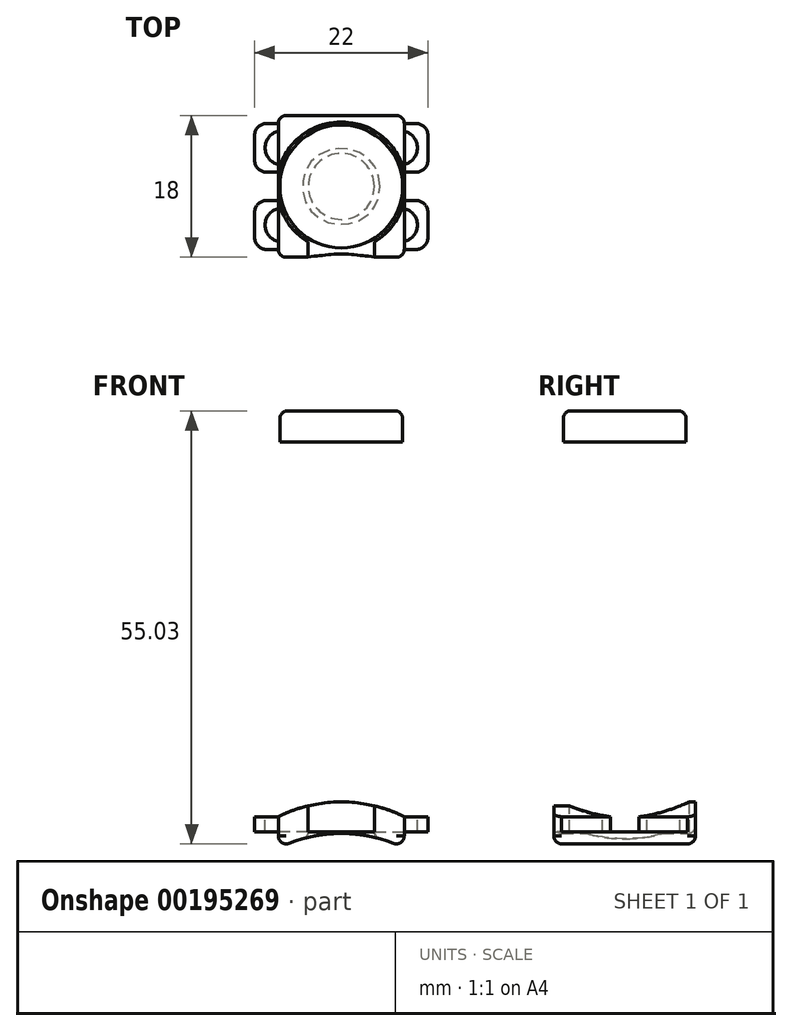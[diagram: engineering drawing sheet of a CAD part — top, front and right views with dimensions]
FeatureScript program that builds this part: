
annotation { "Feature Type Name" : "Feature", "Feature Type Description" : "" }
export const myFeature = defineFeature(function(context is Context, id is Id, definition is map)
    precondition{}
    {
        {
            var Q0;
            Q0=qCreatedBy(makeId("Front.planeOp"),FACE);
            var sketch = newSketch(context, id + "F0", { "sketchPlane" : qUnion([Q0])});
            skLineSegment(sketch, "E0.left", {"start": v(8, 1.57) * mm, "end": v(8, -1.57) * mm});
            skLineSegment(sketch, "E0.right", {"start": v(-8, 1.57) * mm, "end": v(-8, -1.57) * mm});
            skPoint(sketch, "E0.middle", {"position": v(0, 0) * mm});
            skArc(sketch, "E1", {"start": v(8, -1.57) * mm, "mid": v(0, 0.3) * mm, "end": v(-8, -1.57) * mm});
            skArc(sketch, "E2", {"start": v(8, 2.43) * mm, "mid": v(0, 4.3) * mm, "end": v(-8, 2.43) * mm});
            skLineSegment(sketch, "E3", {"start": v(-8, 1.57) * mm, "end": v(-8, 2.43) * mm});
            skLineSegment(sketch, "E4", {"start": v(8, 1.57) * mm, "end": v(8, 2.43) * mm});
            skLineSegment(sketch, "E5", {"start": v(-8, 2.43) * mm, "end": v(8, 2.43) * mm, "construction": true});
            skLineSegment(sketch, "E6", {"start": v(8, -1.57) * mm, "end": v(-8, -1.57) * mm, "construction": true});
            skSolve(sketch);
        }
        {
            var Q0;
            Q0=qSketchRegion(id+"F0",true);
            extrude(context, id + "F1", {"entities" : qUnion([Q0]), "endBound" : BoundingType.SYMMETRIC, "depth" : 18 * mm});
        }
        {
            var Q0;
            Q0=qCreatedBy(makeId("Top.planeOp"),FACE);
            cPlane(context, id + "F2", {"entities" : qUnion([Q0]), "cplaneType" : CPlaneType.OFFSET, "offset" : 25 * mm, "width" : 150 * mm, "height" : 150 * mm});
        }
        {
            var Q0;
            Q0=qCreatedBy(id+"F2.planeOp",FACE);
            var sketch = newSketch(context, id + "F3", { "sketchPlane" : qUnion([Q0])});
            skCircle(sketch, "E7", {"center": v(0, 0) * mm, "radius": 4.2 * mm});
            skArc(sketch, "E8", {"start": v(4.2, -7.04) * mm, "mid": v(0, 8.2) * mm, "end": v(-4.2, -7.04) * mm});
            skLineSegment(sketch, "E9.top", {"start": v(-4.2, -9) * mm, "end": v(4.2, -9) * mm});
            skLineSegment(sketch, "E9.left", {"start": v(-4.2, -7.04) * mm, "end": v(-4.2, -9) * mm});
            skLineSegment(sketch, "E9.right", {"start": v(4.2, -7.04) * mm, "end": v(4.2, -9) * mm});
            skSolve(sketch);
        }
        {
            var Q0;
            Q0=makeQuery(id+"F3.imprint","IMPRINT",FACE,{"disambiguationData":[TD([[makeQuery(id+"F3.imprint","IMPRINT",EDGE,{"derivedFrom":sQuery(id+"F3.wireOp",EDGE,"E7")}),1.0]])]});
            extrude(context, id + "F4", {"entities" : qUnion([Q0]), "operationType" : NewBodyOperationType.REMOVE, "endBound" : BoundingType.THROUGH_ALL, "oppositeDirection" : true, "depth" : 25 * mm});
        }
        {
            var Q0;
            Q0=makeQuery(id+"F3.imprint","IMPRINT",FACE,{"disambiguationData":[TD([[makeQuery(id+"F3.imprint","IMPRINT",EDGE,{"derivedFrom":sQuery(id+"F3.wireOp",EDGE,"E7")}),-1.0]])]});
            extrude(context, id + "F5", {"entities" : qUnion([Q0]), "operationType" : NewBodyOperationType.REMOVE, "oppositeDirection" : true, "depth" : 24.5 * mm});
        }
        {
            var Q0;
            Q0=qCreatedBy(id+"F2.planeOp",FACE);
            cPlane(context, id + "F6", {"entities" : qUnion([Q0]), "cplaneType" : CPlaneType.OFFSET, "offset" : 25 * mm, "width" : 150 * mm, "height" : 150 * mm});
        }
        {
            var Q0;
            Q0=qCreatedBy(id+"F6.planeOp",FACE);
            var sketch = newSketch(context, id + "F7", { "sketchPlane" : qUnion([Q0])});
            skCircle(sketch, "E10", {"center": v(0, 0) * mm, "radius": 7.8 * mm});
            skSolve(sketch);
        }
        {
            var Q0;
            Q0=makeQuery(id+"F7.imprint","IMPRINT",FACE,{"disambiguationData":[TD([[makeQuery(id+"F7.imprint","IMPRINT",EDGE,{"derivedFrom":sQuery(id+"F7.wireOp",EDGE,"E10")}),1.0]])]});
            extrude(context, id + "F8", {"entities" : qUnion([Q0]), "depth" : 4 * mm});
        }
        {
            var Q0;
            Q0=makeQuery(id+"F1.opExtrude","CAP_EDGE",EDGE,{"disambiguationData":[OSD([sQuery(id+"F0.wireOp",EDGE,"E0.left"),sQuery(id+"F0.wireOp",EDGE,"E4")])],"isStart":false});
            var Q1;
            Q1=makeQuery(id+"F1.opExtrude","CAP_EDGE",EDGE,{"disambiguationData":[OSD([sQuery(id+"F0.wireOp",EDGE,"E0.left"),sQuery(id+"F0.wireOp",EDGE,"E4")])],"isStart":true});
            var Q2;
            Q2=makeQuery(id+"F1.opExtrude","CAP_EDGE",EDGE,{"disambiguationData":[OSD([sQuery(id+"F0.wireOp",EDGE,"E0.right"),sQuery(id+"F0.wireOp",EDGE,"E3")])],"isStart":false});
            var Q3;
            Q3=makeQuery(id+"F1.opExtrude","CAP_EDGE",EDGE,{"disambiguationData":[OSD([sQuery(id+"F0.wireOp",EDGE,"E0.right"),sQuery(id+"F0.wireOp",EDGE,"E3")])],"isStart":true});
            var Q4;
            Q4=makeQuery(id+"F8.opExtrude","CAP_EDGE",EDGE,{"disambiguationData":[OSD([sQuery(id+"F7.wireOp",EDGE,"E10")])],"isStart":false});
            fillet(context, id + "F9", {"entities" : qUnion([Q0, Q1, Q2, Q3, Q4]), "radius" : 1 * mm, "tangentPropagation" : true, "allowEdgeOverflow" : false});
        }
        {
            var Q0;
            Q0=makeQuery(id+"F1.opExtrude","SWEPT_EDGE",EDGE,{"disambiguationData":[OSD([sQuery(id+"F0.wireOp",EDGE,"E0.right"),sQuery(id+"F0.wireOp",EDGE,"E1")])]});
            var Q1;
            Q1=makeQuery(id+"F4.boolean.opBoolean","INTERSECT",EDGE,{"derivedFrom":[makeQuery(id+"F1.opExtrude","SWEPT_FACE",FACE,{"disambiguationData":[OSD([sQuery(id+"F0.wireOp",EDGE,"E1")])]}),makeQuery(id+"F4.opExtrude","SWEPT_FACE",FACE,{"disambiguationData":[OSD([sQuery(id+"F3.wireOp",EDGE,"E7")])]})]});
            fillet(context, id + "F10", {"entities" : qUnion([Q0, Q1]), "radius" : 1 * mm, "tangentPropagation" : true, "allowEdgeOverflow" : false});
        }
        {
            var Q0;
            Q0=makeQuery(id+"F1.opExtrude","SWEPT_FACE",FACE,{"disambiguationData":[OSD([sQuery(id+"F0.wireOp",EDGE,"E0.left"),sQuery(id+"F0.wireOp",EDGE,"E4")])]});
            var sketch = newSketch(context, id + "F11", { "sketchPlane" : qUnion([Q0])});
            skLineSegment(sketch, "E11.bottom", {"start": v(-8, 2.43) * mm, "end": v(-1.8, 2.43) * mm});
            skLineSegment(sketch, "E11.top", {"start": v(-8, 0.5) * mm, "end": v(-1.8, 0.5) * mm});
            skLineSegment(sketch, "E11.left", {"start": v(-8, 2.43) * mm, "end": v(-8, 0.5) * mm});
            skLineSegment(sketch, "E11.right", {"start": v(-1.8, 2.43) * mm, "end": v(-1.8, 0.5) * mm});
            skLineSegment(sketch, "E12.bottom", {"start": v(8, 2.43) * mm, "end": v(1.8, 2.43) * mm});
            skLineSegment(sketch, "E12.top", {"start": v(8, 0.5) * mm, "end": v(1.8, 0.5) * mm});
            skLineSegment(sketch, "E12.left", {"start": v(8, 2.43) * mm, "end": v(8, 0.5) * mm});
            skLineSegment(sketch, "E12.right", {"start": v(1.8, 2.43) * mm, "end": v(1.8, 0.5) * mm});
            skSolve(sketch);
        }
        {
            var Q0;
            Q0 = qSketchRegion(id + "F11", true);
            extrude(context, id + "F12", {"entities" : qUnion([Q0]), "operationType" : NewBodyOperationType.ADD, "depth" : 3 * mm});
        }
        {
            var Q0;
            Q0=makeQuery(id+"F12.opExtrude","SWEPT_FACE",FACE,{"disambiguationData":[OSD([sQuery(id+"F11.wireOp",EDGE,"E12.bottom")])]});
            var sketch = newSketch(context, id + "F13", { "sketchPlane" : qUnion([Q0])});
            skArc(sketch, "E13", {"start": v(8, 2.8) * mm, "mid": v(9.68, 4.9) * mm, "end": v(8, 7) * mm});
            skLineSegment(sketch, "E14", {"start": v(8, 7) * mm, "end": v(8, 2.8) * mm});
            skLineSegment(sketch, "E15", {"start": v(0, 0) * mm, "end": v(22.53, 0) * mm, "construction": true});
            skArc(sketch, "E16.MirrorCS", {"start": v(8, -2.8) * mm, "mid": v(9.68, -4.9) * mm, "end": v(8, -7) * mm});
            skLineSegment(sketch, "E17.MirrorCS", {"start": v(8, -7) * mm, "end": v(8, -2.8) * mm});
            skSolve(sketch);
        }
        {
            var Q0;
            Q0 = qSketchRegion(id + "F13", true);
            var Q1;
            Q1=makeQuery(id+"F12.opExtrude","SWEPT_FACE",FACE,{"disambiguationData":[OSD([sQuery(id+"F11.wireOp",EDGE,"E11.top")])]});
            extrude(context, id + "F14", {"entities" : qUnion([Q0]), "operationType" : NewBodyOperationType.REMOVE, "endBound" : BoundingType.UP_TO_SURFACE, "oppositeDirection" : true, "endBoundEntityFace" : qUnion([Q1]), "depth" : 25 * mm});
        }
        {
            var Q0;
            Q0=makeQuery(id+"F1.opExtrude","SWEPT_FACE",FACE,{"disambiguationData":[OSD([sQuery(id+"F0.wireOp",EDGE,"E0.right"),sQuery(id+"F0.wireOp",EDGE,"E3")])]});
            var sketch = newSketch(context, id + "F15", { "sketchPlane" : qUnion([Q0])});
            skLineSegment(sketch, "E18.bottom", {"start": v(-8, 2.43) * mm, "end": v(-1.8, 2.43) * mm});
            skLineSegment(sketch, "E18.top", {"start": v(-8, 0.5) * mm, "end": v(-1.8, 0.5) * mm});
            skLineSegment(sketch, "E18.left", {"start": v(-8, 2.43) * mm, "end": v(-8, 0.5) * mm});
            skLineSegment(sketch, "E18.right", {"start": v(-1.8, 2.43) * mm, "end": v(-1.8, 0.5) * mm});
            skLineSegment(sketch, "E19.bottom", {"start": v(8, 2.43) * mm, "end": v(1.8, 2.43) * mm});
            skLineSegment(sketch, "E19.top", {"start": v(8, 0.5) * mm, "end": v(1.8, 0.5) * mm});
            skLineSegment(sketch, "E19.left", {"start": v(8, 2.43) * mm, "end": v(8, 0.5) * mm});
            skLineSegment(sketch, "E19.right", {"start": v(1.8, 2.43) * mm, "end": v(1.8, 0.5) * mm});
            skSolve(sketch);
        }
        {
            var Q0;
            Q0 = qSketchRegion(id + "F15", true);
            extrude(context, id + "F16", {"entities" : qUnion([Q0]), "operationType" : NewBodyOperationType.ADD, "depth" : 3 * mm});
        }
        {
            var Q0;
            Q0=makeQuery(id+"F16.opExtrude","SWEPT_FACE",FACE,{"disambiguationData":[OSD([sQuery(id+"F15.wireOp",EDGE,"E18.bottom")])]});
            var sketch = newSketch(context, id + "F17", { "sketchPlane" : qUnion([Q0])});
            skArc(sketch, "E20", {"start": v(8, -7) * mm, "mid": v(9.68, -4.9) * mm, "end": v(8, -2.8) * mm, "construction": true});
            skLineSegment(sketch, "E21", {"start": v(8, -2.8) * mm, "end": v(8, -7) * mm, "construction": true});
            skLineSegment(sketch, "E22", {"start": v(-25.08, 0) * mm, "end": v(-2.56, 0) * mm, "construction": true});
            skArc(sketch, "E23.MirrorCS", {"start": v(8, 7) * mm, "mid": v(9.68, 4.9) * mm, "end": v(8, 2.8) * mm, "construction": true});
            skLineSegment(sketch, "E24.MirrorCS", {"start": v(8, 2.8) * mm, "end": v(8, 7) * mm, "construction": true});
            skLineSegment(sketch, "E25", {"start": v(0, 13.3) * mm, "end": v(0, -13.53) * mm, "construction": true});
            skLineSegment(sketch, "E26.MirrorCS", {"start": v(-8, 2.8) * mm, "end": v(-8, 7) * mm});
            skLineSegment(sketch, "E27.MirrorCS", {"start": v(-8, -2.8) * mm, "end": v(-8, -7) * mm});
            skArc(sketch, "E28.MirrorCS", {"start": v(-8, 7) * mm, "mid": v(-9.68, 4.9) * mm, "end": v(-8, 2.8) * mm});
            skArc(sketch, "E29.MirrorCS", {"start": v(-8, -7) * mm, "mid": v(-9.68, -4.9) * mm, "end": v(-8, -2.8) * mm});
            skSolve(sketch);
        }
        {
            var Q0;
            Q0 = qSketchRegion(id + "F17", true);
            var Q1;
            Q1=makeQuery(id+"F16.opExtrude","SWEPT_FACE",FACE,{"disambiguationData":[OSD([sQuery(id+"F15.wireOp",EDGE,"E19.top")])]});
            extrude(context, id + "F18", {"entities" : qUnion([Q0]), "operationType" : NewBodyOperationType.REMOVE, "endBound" : BoundingType.UP_TO_SURFACE, "oppositeDirection" : true, "endBoundEntityFace" : qUnion([Q1]), "depth" : 25 * mm});
        }
        {
            var Q0;
            Q0=makeQuery(id+"F12.opExtrude","CAP_EDGE",EDGE,{"disambiguationData":[OSD([sQuery(id+"F11.wireOp",EDGE,"E11.left")])],"isStart":false});
            var Q1;
            Q1=makeQuery(id+"F12.opExtrude","CAP_EDGE",EDGE,{"disambiguationData":[OSD([sQuery(id+"F11.wireOp",EDGE,"E11.right")])],"isStart":false});
            var Q2;
            Q2=makeQuery(id+"F12.opExtrude","CAP_EDGE",EDGE,{"disambiguationData":[OSD([sQuery(id+"F11.wireOp",EDGE,"E12.right")])],"isStart":false});
            var Q3;
            Q3=makeQuery(id+"F12.opExtrude","CAP_EDGE",EDGE,{"disambiguationData":[OSD([sQuery(id+"F11.wireOp",EDGE,"E12.left")])],"isStart":false});
            var Q4;
            Q4=makeQuery(id+"F16.opExtrude","CAP_EDGE",EDGE,{"disambiguationData":[OSD([sQuery(id+"F15.wireOp",EDGE,"E19.left")])],"isStart":false});
            var Q5;
            Q5=makeQuery(id+"F16.opExtrude","CAP_EDGE",EDGE,{"disambiguationData":[OSD([sQuery(id+"F15.wireOp",EDGE,"E19.right")])],"isStart":false});
            var Q6;
            Q6=makeQuery(id+"F16.opExtrude","CAP_EDGE",EDGE,{"disambiguationData":[OSD([sQuery(id+"F15.wireOp",EDGE,"E18.right")])],"isStart":false});
            var Q7;
            Q7=makeQuery(id+"F16.opExtrude","CAP_EDGE",EDGE,{"disambiguationData":[OSD([sQuery(id+"F15.wireOp",EDGE,"E18.left")])],"isStart":false});
            fillet(context, id + "F19", {"entities" : qUnion([Q0, Q1, Q2, Q3, Q4, Q5, Q6, Q7]), "radius" : 1.5 * mm, "tangentPropagation" : true, "allowEdgeOverflow" : false});
        }
    });
